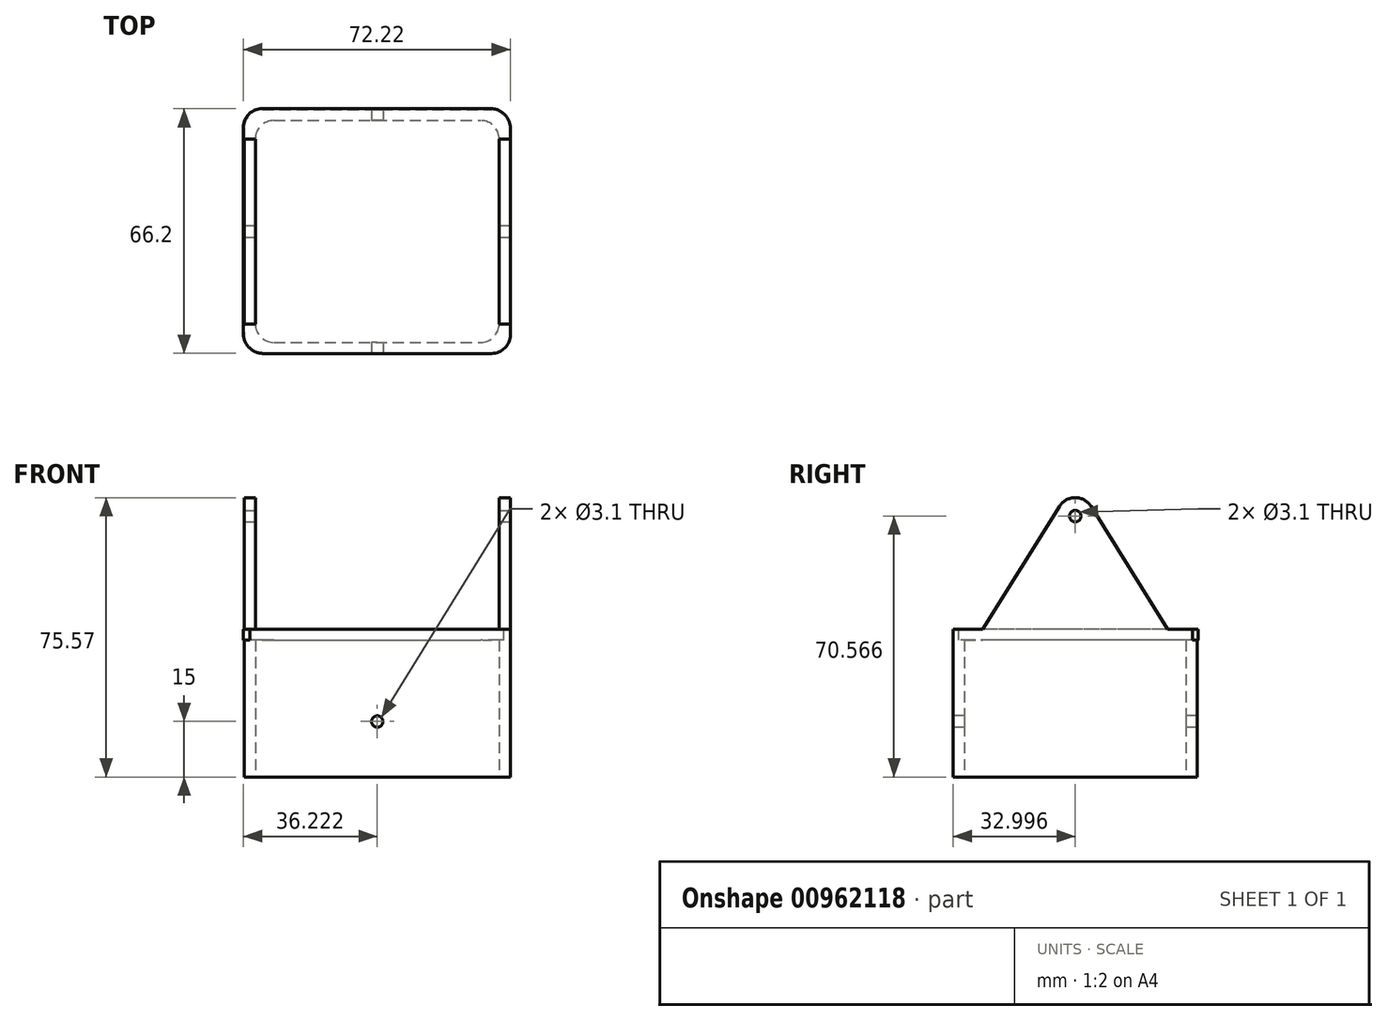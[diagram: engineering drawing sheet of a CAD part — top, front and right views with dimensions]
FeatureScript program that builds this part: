
annotation { "Feature Type Name" : "Feature", "Feature Type Description" : "" }
export const myFeature = defineFeature(function(context is Context, id is Id, definition is map)
    precondition{}
    {
        {
            var Q0;
            Q0=qCreatedBy(makeId("Top.planeOp"),FACE);
            var sketch = newSketch(context, id + "F0", { "sketchPlane" : qUnion([Q0])});
            skLineSegment(sketch, "E0.bottom", {"start": v(-1241.02, 753.28) * mm, "end": v(1259.52, 753.28) * mm});
            skLineSegment(sketch, "E0.top", {"start": v(-1241.02, -770.72) * mm, "end": v(1259.52, -770.72) * mm});
            skLineSegment(sketch, "E0.left", {"start": v(-1241.02, 753.28) * mm, "end": v(-1241.02, -770.72) * mm});
            skLineSegment(sketch, "E0.right", {"start": v(1259.52, 753.28) * mm, "end": v(1259.52, -770.72) * mm});
            skLineSegment(sketch, "E1.bottom", {"start": v(-95.16, -71.78) * mm, "end": v(-39.16, -71.78) * mm});
            skLineSegment(sketch, "E1.top", {"start": v(-95.16, -131.78) * mm, "end": v(-39.16, -131.78) * mm});
            skLineSegment(sketch, "E1.left", {"start": v(-100.16, -76.78) * mm, "end": v(-100.16, -126.78) * mm});
            skLineSegment(sketch, "E1.right", {"start": v(-34.16, -76.78) * mm, "end": v(-34.16, -126.78) * mm});
            skLineSegment(sketch, "E2.0", {"start": v(-103.16, -73.78) * mm, "end": v(-103.16, -129.78) * mm});
            skLineSegment(sketch, "E2.1", {"start": v(-98.16, -68.78) * mm, "end": v(-36.16, -68.78) * mm});
            skLineSegment(sketch, "E2.2", {"start": v(-31.16, -73.78) * mm, "end": v(-31.16, -129.78) * mm});
            skLineSegment(sketch, "E2.3", {"start": v(-98.16, -134.78) * mm, "end": v(-36.16, -134.78) * mm});
            skPoint(sketch, "E3.visualSharp", {"position": v(-100.16, -71.78) * mm});
            skArc(sketch, "E3.filletArc", {"start": v(-95.16, -71.78) * mm, "mid": v(-98.7, -73.25) * mm, "end": v(-100.16, -76.78) * mm});
            skPoint(sketch, "E4.visualSharp", {"position": v(-34.16, -71.78) * mm});
            skArc(sketch, "E4.filletArc", {"start": v(-34.16, -76.78) * mm, "mid": v(-35.62, -73.25) * mm, "end": v(-39.16, -71.78) * mm});
            skPoint(sketch, "E5.visualSharp", {"position": v(-100.16, -131.78) * mm});
            skArc(sketch, "E5.filletArc", {"start": v(-100.16, -126.78) * mm, "mid": v(-98.7, -130.32) * mm, "end": v(-95.16, -131.78) * mm});
            skPoint(sketch, "E6.visualSharp", {"position": v(-34.16, -131.78) * mm});
            skArc(sketch, "E6.filletArc", {"start": v(-39.16, -131.78) * mm, "mid": v(-35.62, -130.32) * mm, "end": v(-34.16, -126.78) * mm});
            skPoint(sketch, "E7.visualSharp", {"position": v(-103.16, -68.78) * mm});
            skArc(sketch, "E7.filletArc", {"start": v(-98.16, -68.78) * mm, "mid": v(-101.7, -70.25) * mm, "end": v(-103.16, -73.78) * mm});
            skPoint(sketch, "E8.visualSharp", {"position": v(-31.16, -68.78) * mm});
            skArc(sketch, "E8.filletArc", {"start": v(-31.16, -73.78) * mm, "mid": v(-32.62, -70.25) * mm, "end": v(-36.16, -68.78) * mm});
            skPoint(sketch, "E9.visualSharp", {"position": v(-31.16, -134.78) * mm});
            skArc(sketch, "E9.filletArc", {"start": v(-36.16, -134.78) * mm, "mid": v(-32.62, -133.32) * mm, "end": v(-31.16, -129.78) * mm});
            skPoint(sketch, "E10.visualSharp", {"position": v(-103.16, -134.78) * mm});
            skArc(sketch, "E10.filletArc", {"start": v(-103.16, -129.78) * mm, "mid": v(-101.7, -133.32) * mm, "end": v(-98.16, -134.78) * mm});
            skSolve(sketch);
        }
        {
            var Q0;
            Q0=makeQuery(id+"F0.imprint","IMPRINT",FACE,{"disambiguationData":[TD([[makeQuery(id+"F0.imprint","IMPRINT",EDGE,{"derivedFrom":sQuery(id+"F0.wireOp",EDGE,"E1.bottom")}),1.0]])]});
            extrude(context, id + "F1", {"entities" : qUnion([Q0]), "depth" : 40 * mm, "offsetDistance" : 25 * mm});
        }
        {
            var Q0;
            Q0=makeQuery(id+"F1.opExtrude","SWEPT_FACE",FACE,{"disambiguationData":[OSD([sQuery(id+"F0.wireOp",EDGE,"E1.left")])]});
            var sketch = newSketch(context, id + "F2", { "sketchPlane" : qUnion([Q0])});
            skLineSegment(sketch, "E11", {"start": v(-126.78, 40) * mm, "end": v(-106.02, 73.22) * mm});
            skLineSegment(sketch, "E12", {"start": v(-76.78, 40) * mm, "end": v(-97.54, 73.22) * mm});
            skPoint(sketch, "E13.start.orphan", {"position": v(-101.78, 40) * mm});
            skPoint(sketch, "E14.visualSharp", {"position": v(-101.78, 80) * mm});
            skArc(sketch, "E14.filletArc", {"start": v(-97.54, 73.22) * mm, "mid": v(-101.78, 75.57) * mm, "end": v(-106.02, 73.22) * mm});
            skSolve(sketch);
        }
        {
            var Q0;
            Q0 = qSketchRegion(id + "F2", true);
            var Q1;
            Q1=makeQuery(id+"F2.imprint","IMPRINT",FACE,{"disambiguationData":[TD([[makeQuery(id+"F2.imprint","IMPRINT",EDGE,{"derivedFrom":sQuery(id+"F2.wireOp",EDGE,"E11")}),-1.0]])]});
            extrude(context, id + "F3", {"entities" : qUnion([Q0, Q1]), "operationType" : NewBodyOperationType.ADD, "oppositeDirection" : true, "depth" : 3 * mm, "offsetDistance" : 25 * mm});
        }
        {
            var Q0;
            Q0=makeQuery(id+"F1.opExtrude","SWEPT_FACE",FACE,{"disambiguationData":[OSD([sQuery(id+"F0.wireOp",EDGE,"E1.right")])]});
            var sketch = newSketch(context, id + "F4", { "sketchPlane" : qUnion([Q0])});
            skLineSegment(sketch, "E15", {"start": v(76.78, 40) * mm, "end": v(97.54, 73.22) * mm});
            skLineSegment(sketch, "E16", {"start": v(126.78, 40) * mm, "end": v(106.02, 73.22) * mm});
            skLineSegment(sketch, "E17", {"start": v(126.78, 40) * mm, "end": v(80.84, 40) * mm});
            skPoint(sketch, "E18.start.orphan", {"position": v(101.78, 40) * mm});
            skPoint(sketch, "E19.visualSharp", {"position": v(101.78, 80) * mm});
            skArc(sketch, "E19.filletArc", {"start": v(106.02, 73.22) * mm, "mid": v(101.78, 75.57) * mm, "end": v(97.54, 73.22) * mm});
            skSolve(sketch);
        }
        {
            var Q0;
            {var subQ1=sQuery(id+"F4.wireOp",EDGE,"E15");Q0=makeQuery(id+"F4.imprint","IMPRINT",FACE,{"disambiguationData":[TD([[makeQuery(id+"F4.imprint","IMPRINT",EDGE,{"derivedFrom":subQ1}),-1.0]])]});}
            extrude(context, id + "F5", {"entities" : qUnion([Q0]), "operationType" : NewBodyOperationType.ADD, "oppositeDirection" : true, "depth" : 3 * mm, "offsetDistance" : 25 * mm});
        }
        {
            var Q0;
            {var subQ0=sQuery(id+"F0.wireOp",EDGE,"E6.filletArc");var subQ1=sQuery(id+"F0.wireOp",EDGE,"E5.filletArc");var subQ2=sQuery(id+"F0.wireOp",EDGE,"E2.3");var subQ3=sQuery(id+"F0.wireOp",EDGE,"E2.2");var subQ4=sQuery(id+"F0.wireOp",EDGE,"E1.top");var subQ5=sQuery(id+"F0.wireOp",EDGE,"E1.left");var subQ7=sQuery(id+"F0.wireOp",EDGE,"E9.filletArc");var subQ8=sQuery(id+"F0.wireOp",EDGE,"E1.right");var subQ11=sQuery(id+"F0.wireOp",EDGE,"E10.filletArc");var subQ12=sQuery(id+"F0.wireOp",EDGE,"E2.0");Q0=makeQuery(id+"F5.boolean.opBoolean","SPLIT",FACE,{"disambiguationData":[TD([makeQuery(id+"F1.opExtrude","SWEPT_FACE",FACE,{"disambiguationData":[OSD([subQ4])]})])],"derivedFrom":makeQuery(id+"F1.opExtrude","CAP_FACE",FACE,{"disambiguationData":[OSD([sQuery(id+"F0.wireOp",EDGE,"E1.bottom"),subQ4,subQ5,subQ8,subQ12,sQuery(id+"F0.wireOp",EDGE,"E2.1"),subQ3,subQ2,sQuery(id+"F0.wireOp",EDGE,"E3.filletArc"),sQuery(id+"F0.wireOp",EDGE,"E4.filletArc"),subQ1,subQ0,sQuery(id+"F0.wireOp",EDGE,"E7.filletArc"),sQuery(id+"F0.wireOp",EDGE,"E8.filletArc"),subQ7,subQ11])],"isStart":false})});}
            var sketch = newSketch(context, id + "F6", { "sketchPlane" : qUnion([Q0])});
            skLineSegment(sketch, "E20.bottom", {"start": v(-98.38, -68.58) * mm, "end": v(-36.38, -68.58) * mm});
            skLineSegment(sketch, "E20.top", {"start": v(-98.38, -134.58) * mm, "end": v(-36.38, -134.58) * mm});
            skLineSegment(sketch, "E20.left", {"start": v(-103.38, -73.58) * mm, "end": v(-103.38, -129.58) * mm});
            skLineSegment(sketch, "E20.right", {"start": v(-31.38, -73.58) * mm, "end": v(-31.38, -129.58) * mm});
            skPoint(sketch, "E21.visualSharp", {"position": v(-103.38, -68.58) * mm});
            skArc(sketch, "E21.filletArc", {"start": v(-98.38, -68.58) * mm, "mid": v(-101.91, -70.04) * mm, "end": v(-103.38, -73.58) * mm});
            skPoint(sketch, "E22.visualSharp", {"position": v(-31.38, -68.58) * mm});
            skArc(sketch, "E22.filletArc", {"start": v(-31.38, -73.58) * mm, "mid": v(-32.84, -70.04) * mm, "end": v(-36.38, -68.58) * mm});
            skPoint(sketch, "E23.visualSharp", {"position": v(-31.38, -134.58) * mm});
            skArc(sketch, "E23.filletArc", {"start": v(-36.38, -134.58) * mm, "mid": v(-32.84, -133.12) * mm, "end": v(-31.38, -129.58) * mm});
            skPoint(sketch, "E24.visualSharp", {"position": v(-103.38, -134.58) * mm});
            skArc(sketch, "E24.filletArc", {"start": v(-103.38, -129.58) * mm, "mid": v(-101.91, -133.12) * mm, "end": v(-98.38, -134.58) * mm});
            skSolve(sketch);
        }
        {
            var Q0;
            Q0=makeQuery(id+"F6.imprint","IMPRINT",FACE,{"disambiguationData":[TD([[makeQuery(id+"F6.imprint","IMPRINT",EDGE,{"derivedFrom":sQuery(id+"F6.wireOp",EDGE,"E20.bottom")}),-1.0]])]});
            extrude(context, id + "F7", {"entities" : qUnion([Q0]), "operationType" : NewBodyOperationType.ADD, "oppositeDirection" : true, "depth" : 3 * mm, "offsetDistance" : 25 * mm});
        }
        {
            var Q0;
            Q0=makeQuery(id+"F5.boolean.opBoolean","MERGE",FACE,{"derivedFrom":[makeQuery(id+"F1.opExtrude","SWEPT_FACE",FACE,{"disambiguationData":[OSD([sQuery(id+"F0.wireOp",EDGE,"E2.2")])]}),makeQuery(id+"F5.opExtrude","CAP_FACE",FACE,{"disambiguationData":[OSD([sQuery(id+"F0.wireOp",EDGE,"E1.right"),sQuery(id+"F4.wireOp",EDGE,"E15"),sQuery(id+"F4.wireOp",EDGE,"E16"),sQuery(id+"F4.wireOp",EDGE,"E17"),sQuery(id+"F4.wireOp",EDGE,"E19.filletArc")])],"isStart":false})]});
            var sketch = newSketch(context, id + "F8", { "sketchPlane" : qUnion([Q0])});
            skPoint(sketch, "E25", {"position": v(-101.78, 70.57) * mm});
            skSolve(sketch);
        }
        {
            var Q0;
            Q0=sQuery(id+"F8.wireOp",VERTEX,"E25");
            var Q1;
            Q1=makeQuery(id+"F1.opExtrude","SWEPT_BODY",BODY,{"disambiguationData":[OSD([sQuery(id+"F0.wireOp",EDGE,"E1.bottom"),sQuery(id+"F0.wireOp",EDGE,"E1.top"),sQuery(id+"F0.wireOp",EDGE,"E1.left"),sQuery(id+"F0.wireOp",EDGE,"E1.right"),sQuery(id+"F0.wireOp",EDGE,"E2.0"),sQuery(id+"F0.wireOp",EDGE,"E2.1"),sQuery(id+"F0.wireOp",EDGE,"E2.2"),sQuery(id+"F0.wireOp",EDGE,"E2.3"),sQuery(id+"F0.wireOp",EDGE,"E3.filletArc"),sQuery(id+"F0.wireOp",EDGE,"E4.filletArc"),sQuery(id+"F0.wireOp",EDGE,"E5.filletArc"),sQuery(id+"F0.wireOp",EDGE,"E6.filletArc"),sQuery(id+"F0.wireOp",EDGE,"E7.filletArc"),sQuery(id+"F0.wireOp",EDGE,"E8.filletArc"),sQuery(id+"F0.wireOp",EDGE,"E9.filletArc"),sQuery(id+"F0.wireOp",EDGE,"E10.filletArc")])]});
            hole(context, id + "F9", {"style" : HoleStyle.SIMPLE, "endStyle" : HoleEndStyle.THROUGH, "holeDiameter" : 3.1 * mm, "majorDiameter" : 5 * mm, "isTappedThrough" : true, "tappedDepth" : 12 * mm, "tapClearance" : 3, "locations" : qUnion([Q0]), "scope" : qUnion([Q1])});
        }
        {
            var Q0;
            Q0=makeQuery(id+"F1.opExtrude","SWEPT_FACE",FACE,{"disambiguationData":[OSD([sQuery(id+"F0.wireOp",EDGE,"E2.3")])]});
            var sketch = newSketch(context, id + "F10", { "sketchPlane" : qUnion([Q0])});
            skPoint(sketch, "E26", {"position": v(-67.16, 15) * mm});
            skPoint(sketch, "E26.positionSnap0", {"position": v(-67.16, 0) * mm});
            skSolve(sketch);
        }
        {
            var Q0;
            Q0=sQuery(id+"F10.wireOp",VERTEX,"E26");
            var Q1;
            Q1=makeQuery(id+"F1.opExtrude","SWEPT_BODY",BODY,{"disambiguationData":[OSD([sQuery(id+"F0.wireOp",EDGE,"E1.bottom"),sQuery(id+"F0.wireOp",EDGE,"E1.top"),sQuery(id+"F0.wireOp",EDGE,"E1.left"),sQuery(id+"F0.wireOp",EDGE,"E1.right"),sQuery(id+"F0.wireOp",EDGE,"E2.0"),sQuery(id+"F0.wireOp",EDGE,"E2.1"),sQuery(id+"F0.wireOp",EDGE,"E2.2"),sQuery(id+"F0.wireOp",EDGE,"E2.3"),sQuery(id+"F0.wireOp",EDGE,"E3.filletArc"),sQuery(id+"F0.wireOp",EDGE,"E4.filletArc"),sQuery(id+"F0.wireOp",EDGE,"E5.filletArc"),sQuery(id+"F0.wireOp",EDGE,"E6.filletArc"),sQuery(id+"F0.wireOp",EDGE,"E7.filletArc"),sQuery(id+"F0.wireOp",EDGE,"E8.filletArc"),sQuery(id+"F0.wireOp",EDGE,"E9.filletArc"),sQuery(id+"F0.wireOp",EDGE,"E10.filletArc")])]});
            hole(context, id + "F11", {"style" : HoleStyle.SIMPLE, "endStyle" : HoleEndStyle.THROUGH, "holeDiameter" : 3.1 * mm, "majorDiameter" : 5 * mm, "isTappedThrough" : true, "tappedDepth" : 12 * mm, "tapClearance" : 3, "locations" : qUnion([Q0]), "scope" : qUnion([Q1])});
        }
    });
